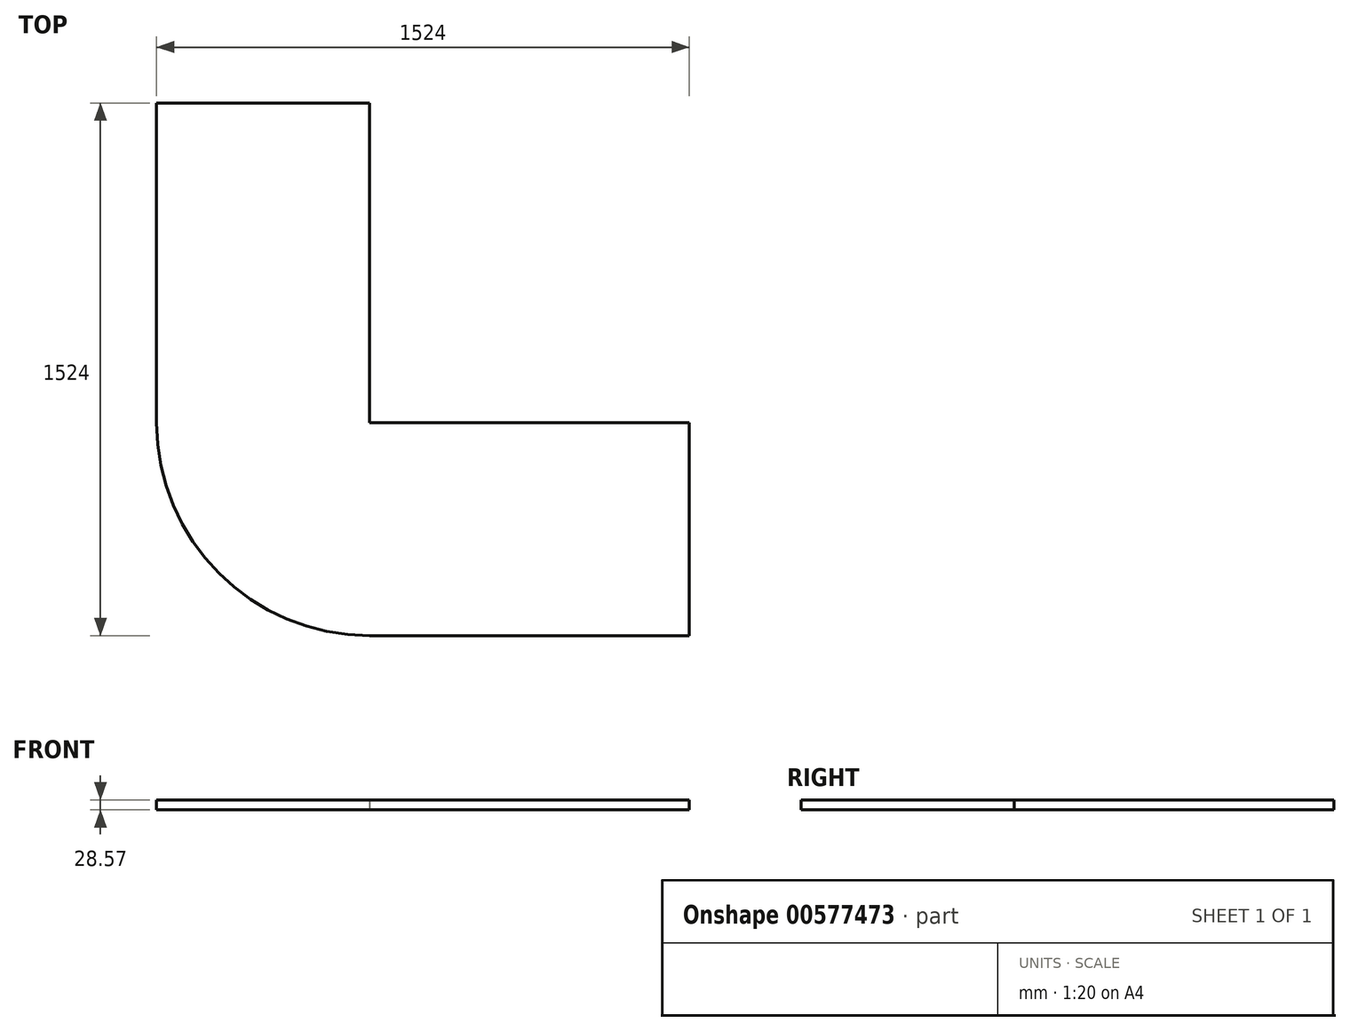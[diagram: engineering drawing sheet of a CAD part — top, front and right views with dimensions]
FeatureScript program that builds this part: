
annotation { "Feature Type Name" : "Feature", "Feature Type Description" : "" }
export const myFeature = defineFeature(function(context is Context, id is Id, definition is map)
    precondition{}
    {
        {
            var Q0;
            Q0=qCreatedBy(makeId("Top.planeOp"),FACE);
            var sketch = newSketch(context, id + "F0", { "sketchPlane" : qUnion([Q0])});
            skLineSegment(sketch, "E0.bottom", {"start": v(304.8, 762) * mm, "end": v(-304.8, 762) * mm});
            skLineSegment(sketch, "E0.top", {"start": v(304.8, -762) * mm, "end": v(-304.8, -762) * mm});
            skLineSegment(sketch, "E0.left", {"start": v(304.8, 762) * mm, "end": v(304.8, -762) * mm});
            skLineSegment(sketch, "E0.right", {"start": v(-304.8, 762) * mm, "end": v(-304.8, -762) * mm});
            skPoint(sketch, "E0.middle", {"position": v(0, 0) * mm});
            skLineSegment(sketch, "E1.bottom", {"start": v(304.8, -762) * mm, "end": v(1219.2, -762) * mm});
            skLineSegment(sketch, "E1.top", {"start": v(304.8, -152.4) * mm, "end": v(1219.2, -152.4) * mm});
            skLineSegment(sketch, "E1.left", {"start": v(304.8, -762) * mm, "end": v(304.8, -152.4) * mm});
            skLineSegment(sketch, "E1.right", {"start": v(1219.2, -762) * mm, "end": v(1219.2, -152.4) * mm});
            skLineSegment(sketch, "E2", {"start": v(304.8, -152.4) * mm, "end": v(609.6, -152.4) * mm});
            skLineSegment(sketch, "E3", {"start": v(609.6, -152.4) * mm, "end": v(609.6, 152.4) * mm});
            skArc(sketch, "E4", {"start": v(609.6, -152.4) * mm, "mid": v(394.07, -63.13) * mm, "end": v(304.8, 152.4) * mm});
            skArc(sketch, "E5", {"start": v(304.8, -762) * mm, "mid": v(-126.25, -583.45) * mm, "end": v(-304.8, -152.4) * mm});
            skSolve(sketch);
        }
        {
            var Q0;
            {var subQ1=sQuery(id+"F0.wireOp",EDGE,"E0.bottom");Q0=makeQuery(id+"F0.imprint","IMPRINT",FACE,{"disambiguationData":[TD([[makeQuery(id+"F0.imprint","IMPRINT",EDGE,{"derivedFrom":subQ1}),1.0]])]});}
            var Q1;
            Q1=makeQuery(id+"F0.imprint","IMPRINT",FACE,{"disambiguationData":[TD([[makeQuery(id+"F0.imprint","IMPRINT",EDGE,{"derivedFrom":sQuery(id+"F0.wireOp",EDGE,"E1.bottom")}),1.0]])]});
            var Q2;
            {var subQ0=sQuery(id+"F0.wireOp",EDGE,"E2");Q2=makeQuery(id+"F0.imprint","IMPRINT",FACE,{"disambiguationData":[TD([[makeQuery(id+"F0.imprint","IMPRINT",EDGE,{"derivedFrom":subQ0}),1.0]])]});}
            extrude(context, id + "F1", {"entities" : qUnion([Q0, Q1, Q2]), "depth" : 28.57 * mm, "offsetDistance" : 25.4 * mm});
        }
    });
